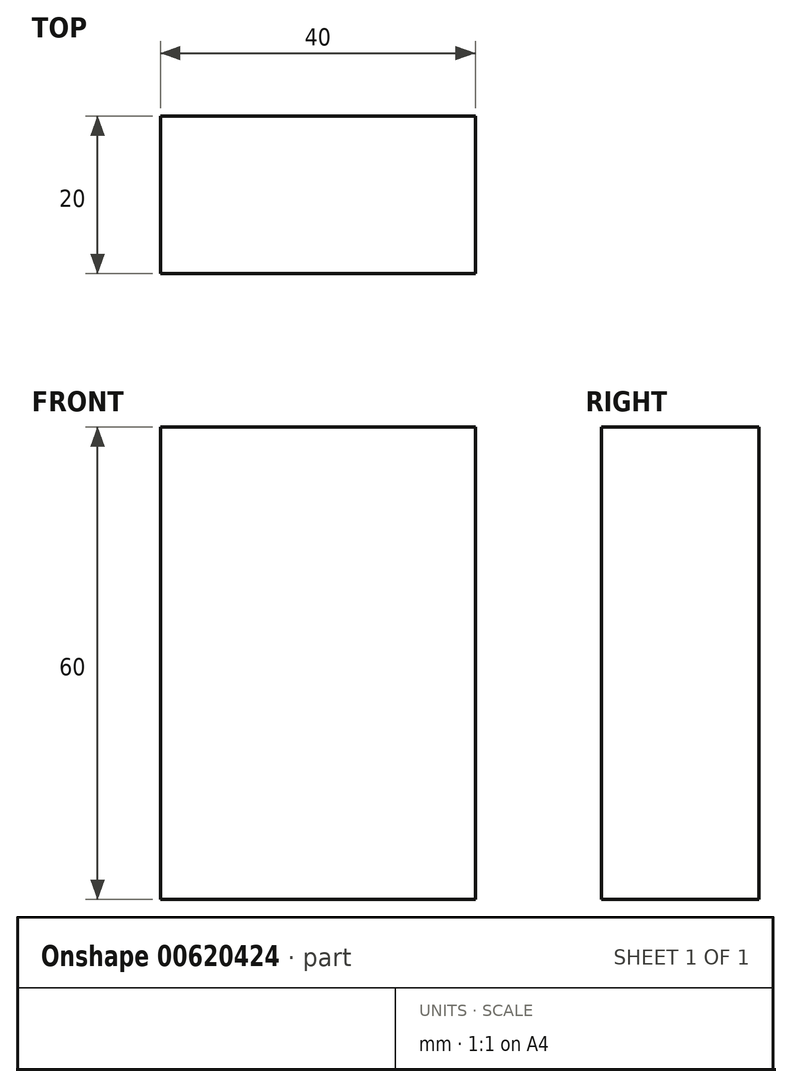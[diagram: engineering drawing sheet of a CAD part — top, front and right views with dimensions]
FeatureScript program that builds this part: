
annotation { "Feature Type Name" : "Feature", "Feature Type Description" : "" }
export const myFeature = defineFeature(function(context is Context, id is Id, definition is map)
    precondition{}
    {
        {
            var Q0;
            Q0=qCreatedBy(makeId("Front.planeOp"),FACE);
            var sketch = newSketch(context, id + "F0", { "sketchPlane" : qUnion([Q0])});
            skLineSegment(sketch, "E0", {"start": v(-65.9, 54.5) * mm, "end": v(-25.9, 54.5) * mm});
            skLineSegment(sketch, "E1", {"start": v(-25.9, 54.5) * mm, "end": v(-25.9, -5.5) * mm});
            skLineSegment(sketch, "E2", {"start": v(-25.9, -5.5) * mm, "end": v(-65.9, -5.5) * mm});
            skLineSegment(sketch, "E3", {"start": v(-65.9, -5.5) * mm, "end": v(-65.9, 54.5) * mm});
            skSolve(sketch);
        }
        {
            var Q0;
            Q0 = qSketchRegion(id + "F0", true);
            extrude(context, id + "F1", {"entities" : qUnion([Q0]), "depth" : 20 * mm, "offsetDistance" : 25 * mm});
        }
    });
